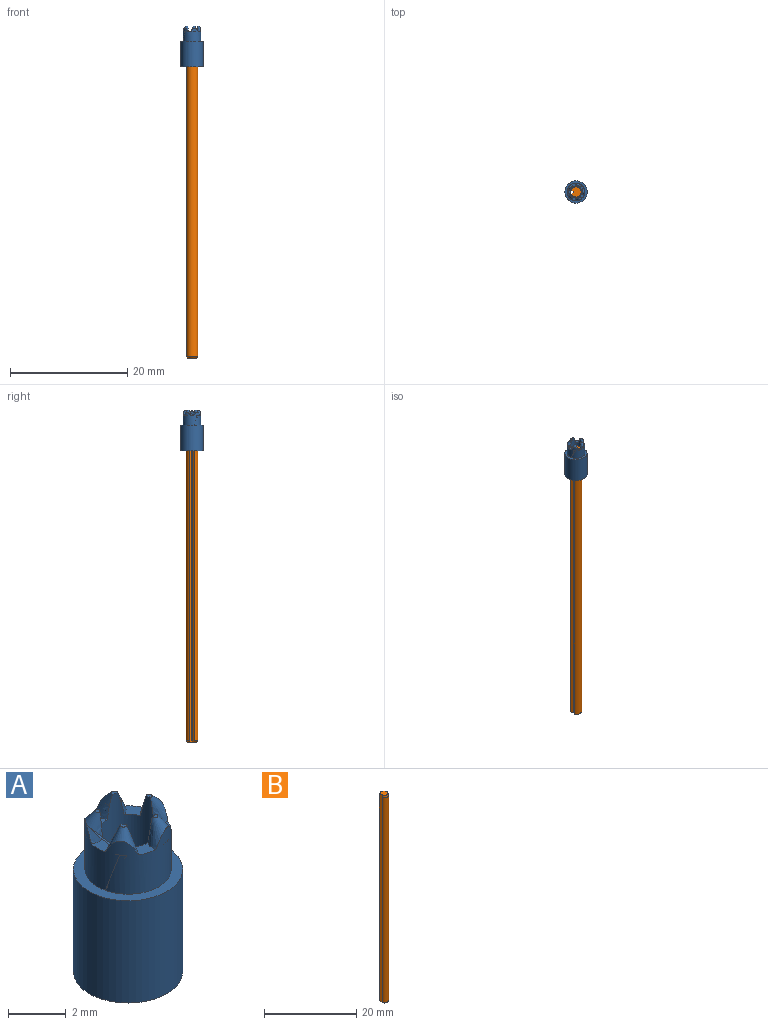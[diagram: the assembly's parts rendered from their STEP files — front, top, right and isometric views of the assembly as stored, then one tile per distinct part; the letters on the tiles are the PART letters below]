
ASSEMBLY  parts=2 mates=1
PART A: 30 faces, bbox 3.9x3.9x7.1 mm
  f0: plane 0.39x0.02mm, normal (0.34,0,-0.94), area 0mm2, adj f4,f5
  f1: cone r=0.6mm half-angle=24.8deg, axis (0.34,0,-0.94), area 1mm2, adj f2,f3,f4,f6,f26
  f2: plane 0.34x0.27mm, normal (0,0,1), area 0mm2, adj f1,f3
  f3: cylinder r=1mm len=6.95mm, axis (0,0,-1), area 39.8mm2, adj f1,f2,f6,f7,f9,f11,f12,f14
  f4: cylinder r=1.5mm len=3mm, axis (0,0,-1), area 17.9mm2, adj f0,f1,f5,f6,f8,f9,f10,f11
  f5: plane 0.38x0.01mm, normal (0,0,1), area 0mm2, adj f0,f4
  f6: plane 0.83x0.8mm, normal (0,0,1), area 0.3mm2, adj f1,f3,f4,f9
  f7: plane 0.34x0.3mm, normal (0,0,1), area 0mm2, adj f3,f9
  f8: plane 0.37x0.13mm, normal (0.11,0.33,-0.94), area 0mm2, adj f4,f10
  f9: cone r=0.6mm half-angle=24.8deg, axis (0.11,0.33,-0.94), area 1mm2, adj f3,f4,f6,f7,f11
  f10: plane 0.37x0.12mm, normal (0,0,1), area 0mm2, adj f4,f8
  f11: plane 0.78x0.7mm, normal (0,0,1), area 0.3mm2, adj f3,f4,f9,f14
  f12: plane 0.34x0.32mm, normal (0,0,1), area 0mm2, adj f3,f14
  f13: plane 0.32x0.23mm, normal (-0.28,0.2,-0.94), area 0mm2, adj f4,f15
  f14: cone r=0.6mm half-angle=24.8deg, axis (-0.28,0.2,-0.94), area 1mm2, adj f3,f4,f11,f12,f16
  f15: plane 0.31x0.23mm, normal (0,0,1), area 0mm2, adj f4,f13
  f16: plane 0.71x0.57mm, normal (0,0,1), area 0.3mm2, adj f3,f4,f14,f19
  f17: plane 0.34x0.32mm, normal (0,0,1), area 0mm2, adj f3,f19
  f18: plane 0.32x0.23mm, normal (-0.28,-0.2,-0.94), area 0mm2, adj f4,f20
  f19: cone r=0.6mm half-angle=24.8deg, axis (-0.28,-0.2,-0.94), area 1mm2, adj f3,f4,f16,f17,f21
  f20: plane 0.31x0.23mm, normal (0,0,1), area 0mm2, adj f4,f18
  f21: plane 0.78x0.7mm, normal (0,0,1), area 0.3mm2, adj f3,f4,f19,f23
  f22: plane 0.37x0.13mm, normal (0.11,-0.33,-0.94), area 0mm2, adj f4,f25
  f23: cone r=0.6mm half-angle=24.8deg, axis (0.11,-0.33,-0.94), area 1mm2, adj f3,f4,f21,f24,f26
  f24: plane 0.34x0.3mm, normal (0,0,1), area 0mm2, adj f3,f23
  f25: plane 0.37x0.12mm, normal (0,0,1), area 0mm2, adj f4,f22
  f26: plane 0.83x0.8mm, normal (0,0,1), area 0.3mm2, adj f1,f3,f4,f23
  f27: cylinder r=1.9mm len=4.35mm, axis (0,0,1), area 51.9mm2, adj f28,f29
  f28: plane 3.8x3.8mm, normal (0,0,-1), area 8.2mm2, adj f3,f27
  f29: plane 3.8x3.8mm, normal (0,0,1), area 4.3mm2, adj f4,f27
PART B: 8 faces, bbox 1.9x2x55 mm
  f0: cylinder r=0.1mm len=55mm, axis (0,0,-1), area 8.6mm2, adj f1,f3,f4,f5
  f1: plane 55.01x0.42mm, normal (-0.71,0.71,0), area 31.6mm2, adj f0,f2,f4,f5,f6,f7
  f2: cylinder r=1mm len=54.3mm, axis (0,0,-1), area 287mm2, adj f1,f3,f6,f7
  f3: plane 55.01x0.42mm, normal (-0.71,-0.71,0), area 31.6mm2, adj f0,f2,f4,f5,f6,f7
  f4: plane 1.73x1.65mm, normal (0,0,1), area 2.2mm2, adj f0,f1,f3,f7
  f5: plane 1.6x1.53mm, normal (0,0,-1), area 1.9mm2, adj f0,f1,f3,f6
  f6: cone r=1mm half-angle=45deg, axis (0,0,1), area 1.4mm2, adj f1,f2,f3,f5
  f7: cone r=0.87mm half-angle=15deg, axis (0,0,-1), area 2.6mm2, adj f1,f2,f3,f4
PLACE A at identity fixed
PLACE B t=(0,0,-54.05)mm
MATE fastened B.f2 <-> A.f3  axis (0,0,1) through (0,0,0.95)mm
